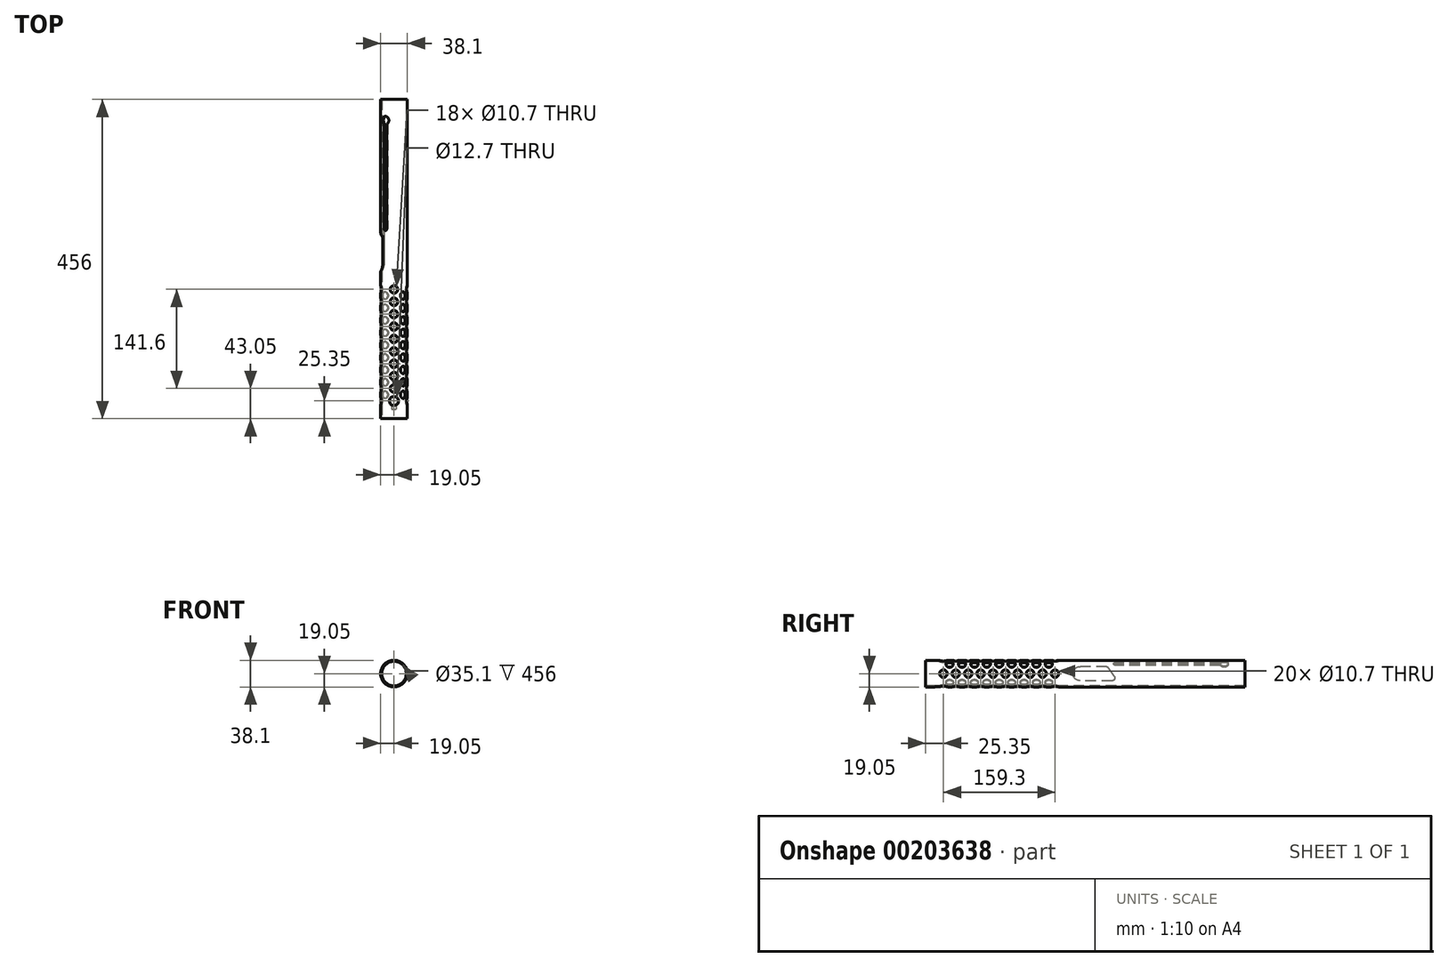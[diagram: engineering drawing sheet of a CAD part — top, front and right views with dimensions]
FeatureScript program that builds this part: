
annotation { "Feature Type Name" : "Feature", "Feature Type Description" : "" }
export const myFeature = defineFeature(function(context is Context, id is Id, definition is map)
    precondition{}
    {
        {
            var Q0;
            Q0=qCreatedBy(makeId("Front.planeOp"),FACE);
            var sketch = newSketch(context, id + "F0", { "sketchPlane" : qUnion([Q0])});
            skCircle(sketch, "E0", {"center": v(0, 0) * mm, "radius": 19.05 * mm});
            skCircle(sketch, "E1.0", {"center": v(0, 0) * mm, "radius": 17.55 * mm});
            skSolve(sketch);
        }
        {
            var Q0;
            Q0 = qSketchRegion(id + "F0", true);
            extrude(context, id + "F1", {"entities" : qUnion([Q0]), "oppositeDirection" : true, "depth" : (266 + 170 + 20) * mm});
        }
        {
            var Q0;
            Q0=qCreatedBy(makeId("Right.planeOp"),FACE);
            var sketch = newSketch(context, id + "F2", { "sketchPlane" : qUnion([Q0])});
            skCircle(sketch, "E2", {"center": v(184.65, 0) * mm, "radius": 5.35 * mm});
            skCircle(sketch, "E3.1.0.0", {"center": v(166.95, 0) * mm, "radius": 5.35 * mm});
            skCircle(sketch, "E3.2.0.0", {"center": v(149.25, 0) * mm, "radius": 5.35 * mm});
            skLineSegment(sketch, "E3.direction1", {"start": v(184.65, 0) * mm, "end": v(166.95, 0) * mm, "construction": true});
            skCircle(sketch, "E4.0.3.0", {"center": v(131.55, 0) * mm, "radius": 5.35 * mm});
            skCircle(sketch, "E4.0.4.0", {"center": v(113.85, 0) * mm, "radius": 5.35 * mm});
            skCircle(sketch, "E4.0.5.0", {"center": v(96.15, 0) * mm, "radius": 5.35 * mm});
            skCircle(sketch, "E4.0.6.0", {"center": v(78.45, 0) * mm, "radius": 5.35 * mm});
            skCircle(sketch, "E4.0.7.0", {"center": v(60.75, 0) * mm, "radius": 5.35 * mm});
            skCircle(sketch, "E4.0.8.0", {"center": v(43.05, 0) * mm, "radius": 5.35 * mm});
            skCircle(sketch, "E4.0.9.0", {"center": v(25.35, 0) * mm, "radius": 5.35 * mm});
            skSolve(sketch);
        }
        {
            var Q0;
            Q0 = qSketchRegion(id + "F2", true);
            extrude(context, id + "F3", {"entities" : qUnion([Q0]), "operationType" : NewBodyOperationType.REMOVE, "endBound" : BoundingType.THROUGH_ALL, "oppositeDirection" : true, "depth" : 25 * mm, "hasSecondDirection" : true, "secondDirectionBound" : SecondDirectionBoundingType.THROUGH_ALL, "secondDirectionOppositeDirection" : false, "secondDirectionDepth" : 25 * mm});
        }
        {
            var Q0;
            Q0=qCreatedBy(makeId("Top.planeOp"),FACE);
            var sketch = newSketch(context, id + "F4", { "sketchPlane" : qUnion([Q0])});
            skCircle(sketch, "E5", {"center": v(0, 184.65) * mm, "radius": 5.35 * mm});
            skCircle(sketch, "E6.0.1.0", {"center": v(0, 166.95) * mm, "radius": 5.35 * mm});
            skLineSegment(sketch, "E6.direction1", {"start": v(0, 184.65) * mm, "end": v(25, 184.65) * mm, "construction": true});
            skLineSegment(sketch, "E6.direction2", {"start": v(0, 184.65) * mm, "end": v(0, 166.95) * mm, "construction": true});
            skCircle(sketch, "E7.0.0.2", {"center": v(0, 149.25) * mm, "radius": 5.35 * mm});
            skCircle(sketch, "E7.0.0.3", {"center": v(0, 131.55) * mm, "radius": 5.35 * mm});
            skCircle(sketch, "E7.0.0.4", {"center": v(0, 113.85) * mm, "radius": 5.35 * mm});
            skCircle(sketch, "E7.0.0.5", {"center": v(0, 96.15) * mm, "radius": 5.35 * mm});
            skCircle(sketch, "E7.0.0.6", {"center": v(0, 78.45) * mm, "radius": 5.35 * mm});
            skCircle(sketch, "E7.0.0.7", {"center": v(0, 60.75) * mm, "radius": 5.35 * mm});
            skCircle(sketch, "E7.0.0.8", {"center": v(0, 43.05) * mm, "radius": 5.35 * mm});
            skCircle(sketch, "E8", {"center": v(0, 25.35) * mm, "radius": 6.35 * mm});
            skSolve(sketch);
        }
        {
            var Q0;
            Q0 = qSketchRegion(id + "F4", true);
            extrude(context, id + "F5", {"entities" : qUnion([Q0]), "operationType" : NewBodyOperationType.REMOVE, "endBound" : BoundingType.THROUGH_ALL, "oppositeDirection" : true, "depth" : 25 * mm, "hasSecondDirection" : true, "secondDirectionBound" : SecondDirectionBoundingType.THROUGH_ALL, "secondDirectionOppositeDirection" : false, "secondDirectionDepth" : 25 * mm});
        }
        {
            var Q0;
            Q0=makeQuery(id+"F1.opExtrude","SWEPT_FACE",FACE,{"disambiguationData":[OSD([sQuery(id+"F0.wireOp",EDGE,"E0")])]});
            cPlane(context, id + "F6", {"entities" : qUnion([Q0]), "cplaneType" : CPlaneType.LINE_ANGLE, "offset" : 25 * mm, "angle" : 45 * degree, "width" : 150 * mm, "height" : 150 * mm});
        }
        {
            var Q0;
            Q0=makeQuery(id+"F1.opExtrude","SWEPT_FACE",FACE,{"disambiguationData":[OSD([sQuery(id+"F0.wireOp",EDGE,"E0")])]});
            cPlane(context, id + "F7", {"entities" : qUnion([Q0]), "cplaneType" : CPlaneType.LINE_ANGLE, "offset" : 25 * mm, "angle" : 315 * degree, "width" : 150 * mm, "height" : 150 * mm});
        }
        {
            var Q0;
            Q0=qCreatedBy(id+"F6.planeOp",FACE);
            var sketch = newSketch(context, id + "F8", { "sketchPlane" : qUnion([Q0])});
            skCircle(sketch, "E9", {"center": v(0, -175.8) * mm, "radius": 5.35 * mm});
            skCircle(sketch, "E10.0.1.0", {"center": v(0, -158.1) * mm, "radius": 5.35 * mm});
            skCircle(sketch, "E10.0.2.0", {"center": v(0, -140.4) * mm, "radius": 5.35 * mm});
            skCircle(sketch, "E10.0.3.0", {"center": v(0, -122.7) * mm, "radius": 5.35 * mm});
            skCircle(sketch, "E10.0.4.0", {"center": v(0, -105) * mm, "radius": 5.35 * mm});
            skCircle(sketch, "E10.0.5.0", {"center": v(0, -87.3) * mm, "radius": 5.35 * mm});
            skCircle(sketch, "E10.0.6.0", {"center": v(0, -69.6) * mm, "radius": 5.35 * mm});
            skCircle(sketch, "E10.0.7.0", {"center": v(0, -51.9) * mm, "radius": 5.35 * mm});
            skCircle(sketch, "E10.0.8.0", {"center": v(0, -34.2) * mm, "radius": 5.35 * mm});
            skLineSegment(sketch, "E10.direction1", {"start": v(0, -175.8) * mm, "end": v(25, -175.8) * mm, "construction": true});
            skLineSegment(sketch, "E10.direction2", {"start": v(0, -175.8) * mm, "end": v(0, -158.1) * mm, "construction": true});
            skSolve(sketch);
        }
        {
            var Q0;
            Q0 = qSketchRegion(id + "F8", true);
            extrude(context, id + "F9", {"entities" : qUnion([Q0]), "operationType" : NewBodyOperationType.REMOVE, "endBound" : BoundingType.THROUGH_ALL, "oppositeDirection" : true, "depth" : 25 * mm, "hasSecondDirection" : true, "secondDirectionBound" : SecondDirectionBoundingType.THROUGH_ALL, "secondDirectionOppositeDirection" : false, "secondDirectionDepth" : 25 * mm});
        }
        {
            var Q0;
            Q0=qCreatedBy(id+"F7.planeOp",FACE);
            var sketch = newSketch(context, id + "F10", { "sketchPlane" : qUnion([Q0])});
            skCircle(sketch, "E11", {"center": v(-175.8, 0) * mm, "radius": 5.35 * mm});
            skCircle(sketch, "E12.1.0.0", {"center": v(-158.1, 0) * mm, "radius": 5.35 * mm});
            skCircle(sketch, "E12.2.0.0", {"center": v(-140.4, 0) * mm, "radius": 5.35 * mm});
            skCircle(sketch, "E12.3.0.0", {"center": v(-122.7, 0) * mm, "radius": 5.35 * mm});
            skCircle(sketch, "E12.4.0.0", {"center": v(-105, 0) * mm, "radius": 5.35 * mm});
            skCircle(sketch, "E12.5.0.0", {"center": v(-87.3, 0) * mm, "radius": 5.35 * mm});
            skCircle(sketch, "E12.6.0.0", {"center": v(-69.6, 0) * mm, "radius": 5.35 * mm});
            skCircle(sketch, "E12.7.0.0", {"center": v(-51.9, 0) * mm, "radius": 5.35 * mm});
            skCircle(sketch, "E12.8.0.0", {"center": v(-34.2, 0) * mm, "radius": 5.35 * mm});
            skLineSegment(sketch, "E12.direction1", {"start": v(-175.8, 0) * mm, "end": v(-158.1, 0) * mm, "construction": true});
            skSolve(sketch);
        }
        {
            var Q0;
            Q0 = qSketchRegion(id + "F10", true);
            extrude(context, id + "F11", {"entities" : qUnion([Q0]), "operationType" : NewBodyOperationType.REMOVE, "endBound" : BoundingType.THROUGH_ALL, "oppositeDirection" : true, "depth" : 25 * mm, "hasSecondDirection" : true, "secondDirectionBound" : SecondDirectionBoundingType.THROUGH_ALL, "secondDirectionOppositeDirection" : false, "secondDirectionDepth" : 25 * mm});
        }
        {
            var Q0;
            Q0=qCreatedBy(makeId("Top.planeOp"),FACE);
            var sketch = newSketch(context, id + "F12", { "sketchPlane" : qUnion([Q0])});
            skCircle(sketch, "E13.0", {"center": v(0, 25.35) * mm, "radius": 6.35 * mm});
            skLineSegment(sketch, "E14.bottom", {"start": v(-3.3, 19.92) * mm, "end": v(3.3, 19.92) * mm});
            skLineSegment(sketch, "E14.top", {"start": v(-3.3, 13.42) * mm, "end": v(3.3, 13.42) * mm});
            skLineSegment(sketch, "E14.left", {"start": v(-3.3, 19.92) * mm, "end": v(-3.3, 13.42) * mm});
            skLineSegment(sketch, "E14.right", {"start": v(3.3, 19.92) * mm, "end": v(3.3, 13.42) * mm});
            skSolve(sketch);
        }
        {
            var Q0;
            Q0 = qSketchRegion(id + "F12", true);
            extrude(context, id + "F13", {"entities" : qUnion([Q0]), "operationType" : NewBodyOperationType.REMOVE, "endBound" : BoundingType.THROUGH_ALL, "oppositeDirection" : true, "depth" : 25 * mm});
        }
        {
            var Q0;
            Q0=qCreatedBy(makeId("Right.planeOp"),FACE);
            var sketch = newSketch(context, id + "F14", { "sketchPlane" : qUnion([Q0])});
            skArc(sketch, "E15", {"start": v(220.52, 10.2) * mm, "mid": v(210.32, 0) * mm, "end": v(220.52, -10.2) * mm});
            skLineSegment(sketch, "E16", {"start": v(220.52, -10.2) * mm, "end": v(266, -10.2) * mm});
            skLineSegment(sketch, "E17", {"start": v(269.28, -3.9) * mm, "end": v(260, 9.34) * mm});
            skLineSegment(sketch, "E18", {"start": v(258.36, 10.2) * mm, "end": v(220.52, 10.2) * mm});
            skPoint(sketch, "E19.visualSharp", {"position": v(259.4, 10.2) * mm});
            skArc(sketch, "E19.filletArc", {"start": v(260, 9.34) * mm, "mid": v(259.29, 9.97) * mm, "end": v(258.36, 10.2) * mm});
            skPoint(sketch, "E20.visualSharp", {"position": v(273.68, -10.2) * mm});
            skArc(sketch, "E20.filletArc", {"start": v(266, -10.2) * mm, "mid": v(269.55, -8.04) * mm, "end": v(269.28, -3.9) * mm});
            skSolve(sketch);
        }
        {
            var Q0;
            Q0 = qSketchRegion(id + "F14", true);
            extrude(context, id + "F15", {"entities" : qUnion([Q0]), "operationType" : NewBodyOperationType.REMOVE, "endBound" : BoundingType.THROUGH_ALL, "oppositeDirection" : true, "depth" : 25 * mm});
        }
        {
            var Q0;
            Q0=makeQuery(id+"F1.opExtrude","SWEPT_FACE",FACE,{"disambiguationData":[OSD([sQuery(id+"F0.wireOp",EDGE,"E0")])]});
            cPlane(context, id + "F16", {"entities" : qUnion([Q0]), "cplaneType" : CPlaneType.LINE_ANGLE, "offset" : 25 * mm, "angle" : 40 * degree, "width" : 150 * mm, "height" : 150 * mm});
        }
        {
            var Q0;
            Q0=qCreatedBy(id+"F16.planeOp",FACE);
            var sketch = newSketch(context, id + "F17", { "sketchPlane" : qUnion([Q0])});
            skCircle(sketch, "E21", {"center": v(0, -426) * mm, "radius": 5.7 * mm});
            skLineSegment(sketch, "E22.bottom", {"start": v(-2.5, -426) * mm, "end": v(2.5, -426) * mm});
            skLineSegment(sketch, "E22.top", {"start": v(0, -268.7) * mm, "end": v(0, -268.7) * mm});
            skLineSegment(sketch, "E22.left", {"start": v(-2.5, -426) * mm, "end": v(-2.5, -271.2) * mm});
            skLineSegment(sketch, "E22.right", {"start": v(2.5, -426) * mm, "end": v(2.5, -271.2) * mm});
            skPoint(sketch, "E23.visualSharp", {"position": v(2.5, -268.7) * mm});
            skArc(sketch, "E23.filletArc", {"start": v(2.5, -271.2) * mm, "mid": v(1.77, -269.43) * mm, "end": v(0, -268.7) * mm});
            skPoint(sketch, "E24.visualSharp", {"position": v(-2.5, -268.7) * mm});
            skArc(sketch, "E24.filletArc", {"start": v(0, -268.7) * mm, "mid": v(-1.77, -269.43) * mm, "end": v(-2.5, -271.2) * mm});
            skSolve(sketch);
        }
        {
            var Q0;
            Q0 = qSketchRegion(id + "F17", true);
            extrude(context, id + "F18", {"entities" : qUnion([Q0]), "operationType" : NewBodyOperationType.REMOVE, "oppositeDirection" : true, "depth" : 25 * mm});
        }
    });
